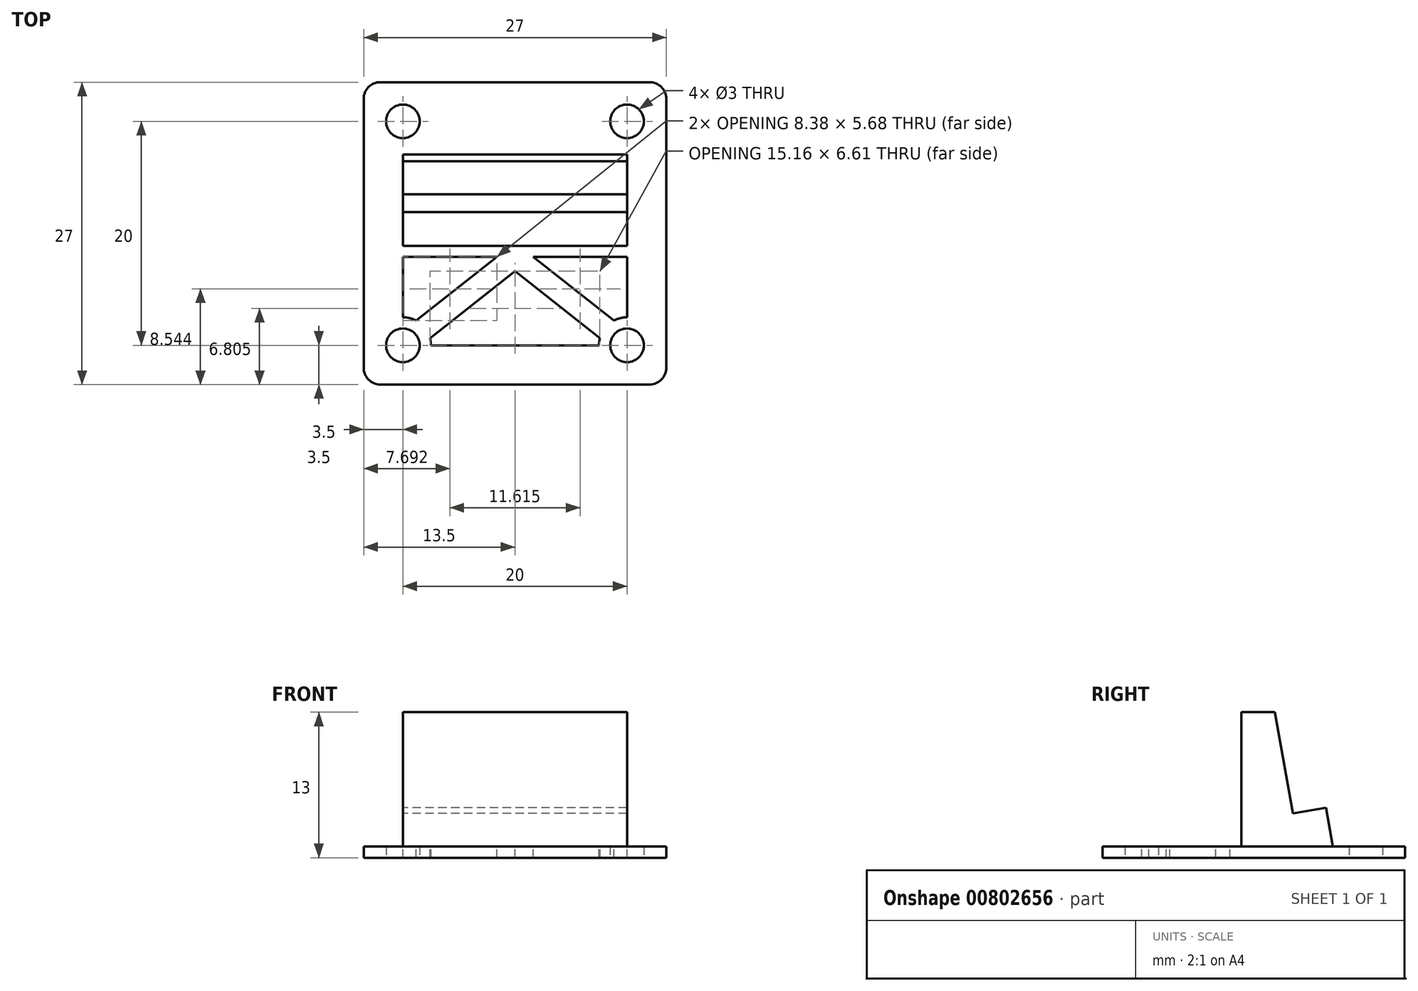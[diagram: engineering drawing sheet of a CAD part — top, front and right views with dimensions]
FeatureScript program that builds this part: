
annotation { "Feature Type Name" : "Feature", "Feature Type Description" : "" }
export const myFeature = defineFeature(function(context is Context, id is Id, definition is map)
    precondition{}
    {
        {
            var Q0;
            Q0=qCreatedBy(makeId("Top.planeOp"),FACE);
            var sketch = newSketch(context, id + "F0", { "sketchPlane" : qUnion([Q0])});
            skLineSegment(sketch, "E0.bottom", {"start": v(-12, 13.5) * mm, "end": v(12, 13.5) * mm});
            skLineSegment(sketch, "E0.top", {"start": v(-12, -13.5) * mm, "end": v(12, -13.5) * mm});
            skLineSegment(sketch, "E0.left", {"start": v(-13.5, 12) * mm, "end": v(-13.5, -12) * mm});
            skLineSegment(sketch, "E0.right", {"start": v(13.5, 12) * mm, "end": v(13.5, -12) * mm});
            skPoint(sketch, "E0.middle", {"position": v(0, 0) * mm});
            skLineSegment(sketch, "E1.bottom", {"start": v(-10, 10) * mm, "end": v(10, 10) * mm, "construction": true});
            skLineSegment(sketch, "E1.top", {"start": v(-10, -10) * mm, "end": v(10, -10) * mm, "construction": true});
            skLineSegment(sketch, "E1.left", {"start": v(-10, 10) * mm, "end": v(-10, -10) * mm, "construction": true});
            skLineSegment(sketch, "E1.right", {"start": v(10, 10) * mm, "end": v(10, -10) * mm, "construction": true});
            skPoint(sketch, "E2.visualSharp", {"position": v(-13.5, 13.5) * mm});
            skArc(sketch, "E2.filletArc", {"start": v(-12, 13.5) * mm, "mid": v(-13.06, 13.06) * mm, "end": v(-13.5, 12) * mm});
            skPoint(sketch, "E3.visualSharp", {"position": v(13.5, 13.5) * mm});
            skArc(sketch, "E3.filletArc", {"start": v(13.5, 12) * mm, "mid": v(13.06, 13.06) * mm, "end": v(12, 13.5) * mm});
            skPoint(sketch, "E4.visualSharp", {"position": v(13.5, -13.5) * mm});
            skArc(sketch, "E4.filletArc", {"start": v(12, -13.5) * mm, "mid": v(13.06, -13.06) * mm, "end": v(13.5, -12) * mm});
            skPoint(sketch, "E5.visualSharp", {"position": v(-13.5, -13.5) * mm});
            skArc(sketch, "E5.filletArc", {"start": v(-13.5, -12) * mm, "mid": v(-13.06, -13.06) * mm, "end": v(-12, -13.5) * mm});
            skSolve(sketch);
        }
        {
            var Q0;
            Q0=makeQuery(id+"F0.imprint","IMPRINT",FACE,{"disambiguationData":[TD([[makeQuery(id+"F0.imprint","IMPRINT",EDGE,{"derivedFrom":sQuery(id+"F0.wireOp",EDGE,"E0.bottom")}),-1.0]])]});
            extrude(context, id + "F1", {"entities" : qUnion([Q0]), "depth" : 1 * mm, "offsetDistance" : 25 * mm});
        }
        {
            var Q0;
            Q0=qCreatedBy(makeId("Right.planeOp"),FACE);
            var sketch = newSketch(context, id + "F2", { "sketchPlane" : qUnion([Q0])});
            skLineSegment(sketch, "E6", {"start": v(3.48, 3.95) * mm, "end": v(1.88, 13) * mm});
            skLineSegment(sketch, "E7", {"start": v(4, 1) * mm, "end": v(7.89, 1) * mm});
            skLineSegment(sketch, "E8", {"start": v(3.48, 3.95) * mm, "end": v(6.43, 4.48) * mm});
            skLineSegment(sketch, "E9", {"start": v(1.88, 13) * mm, "end": v(-1.12, 13) * mm});
            skLineSegment(sketch, "E10", {"start": v(-1.12, 13) * mm, "end": v(-1.12, 1) * mm});
            skLineSegment(sketch, "E11", {"start": v(-1.12, 1) * mm, "end": v(7.89, 1) * mm});
            skLineSegment(sketch, "E12", {"start": v(6.43, 4.48) * mm, "end": v(7.05, 1) * mm});
            skLineSegment(sketch, "E13", {"start": v(7.05, 1) * mm, "end": v(4, 1) * mm});
            skSolve(sketch);
        }
        {
            var Q0;
            Q0=makeQuery(id+"F2.imprint","IMPRINT",FACE,{"disambiguationData":[TD([[makeQuery(id+"F2.imprint","IMPRINT",EDGE,{"derivedFrom":sQuery(id+"F2.wireOp",EDGE,"E6")}),1.0]])]});
            extrude(context, id + "F3", {"entities" : qUnion([Q0]), "operationType" : NewBodyOperationType.ADD, "endBound" : BoundingType.SYMMETRIC, "depth" : 20 * mm, "offsetDistance" : 25 * mm});
        }
        {
            var Q0;
            Q0=sQuery(id+"F0.wireOp",VERTEX,"E1.top.end");
            var Q1;
            Q1=sQuery(id+"F0.wireOp",VERTEX,"E1.top.start");
            var Q2;
            Q2=sQuery(id+"F0.wireOp",VERTEX,"E1.bottom.start");
            var Q3;
            Q3=sQuery(id+"F0.wireOp",VERTEX,"E1.bottom.end");
            var Q4;
            Q4=makeQuery(id+"F1.opExtrude","SWEPT_BODY",BODY,{"disambiguationData":[OSD([sQuery(id+"F0.wireOp",EDGE,"E0.bottom"),sQuery(id+"F0.wireOp",EDGE,"E0.top"),sQuery(id+"F0.wireOp",EDGE,"E0.left"),sQuery(id+"F0.wireOp",EDGE,"E0.right"),sQuery(id+"F0.wireOp",EDGE,"E2.filletArc"),sQuery(id+"F0.wireOp",EDGE,"E3.filletArc"),sQuery(id+"F0.wireOp",EDGE,"E4.filletArc"),sQuery(id+"F0.wireOp",EDGE,"E5.filletArc")])]});
            hole(context, id + "F4", {"style" : HoleStyle.SIMPLE, "endStyle" : HoleEndStyle.BLIND, "oppositeDirection" : true, "holeDiameter" : 3 * mm, "majorDiameter" : 5 * mm, "holeDepth" : 5 * mm, "isTappedThrough" : true, "tappedDepth" : 12 * mm, "tapClearance" : 3, "locations" : qUnion([Q0, Q1, Q2, Q3]), "scope" : qUnion([Q4])});
        }
        {
            var Q0;
            Q0=makeQuery(id+"F1.opExtrude","CAP_FACE",FACE,{"disambiguationData":[OSD([sQuery(id+"F0.wireOp",EDGE,"E0.bottom"),sQuery(id+"F0.wireOp",EDGE,"E0.top"),sQuery(id+"F0.wireOp",EDGE,"E0.left"),sQuery(id+"F0.wireOp",EDGE,"E0.right"),sQuery(id+"F0.wireOp",EDGE,"E2.filletArc"),sQuery(id+"F0.wireOp",EDGE,"E3.filletArc"),sQuery(id+"F0.wireOp",EDGE,"E4.filletArc"),sQuery(id+"F0.wireOp",EDGE,"E5.filletArc")])],"isStart":false});
            var sketch = newSketch(context, id + "F5", { "sketchPlane" : qUnion([Q0])});
            skLineSegment(sketch, "E14.bottom", {"start": v(-7.5, -10) * mm, "end": v(7.5, -10) * mm});
            skLineSegment(sketch, "E14.top", {"start": v(-10, -2.12) * mm, "end": v(-1.62, -2.12) * mm});
            skLineSegment(sketch, "E14.left", {"start": v(-10, -7.5) * mm, "end": v(-10, -2.12) * mm});
            skLineSegment(sketch, "E14.right", {"start": v(10, -7.5) * mm, "end": v(10, -2.12) * mm});
            skArc(sketch, "E15", {"start": v(-7.5, -10) * mm, "mid": v(-7.52, -9.68) * mm, "end": v(-7.58, -9.37) * mm});
            skArc(sketch, "E16", {"start": v(10, -7.5) * mm, "mid": v(9.4, -7.58) * mm, "end": v(8.82, -7.8) * mm});
            skLineSegment(sketch, "E17", {"start": v(0, -2.12) * mm, "end": v(-10, -10) * mm, "construction": true});
            skLineSegment(sketch, "E18", {"start": v(0, -2.12) * mm, "end": v(10, -10) * mm, "construction": true});
            skLineSegment(sketch, "E19.0", {"start": v(-1.62, -2.12) * mm, "end": v(-8.82, -7.8) * mm});
            skLineSegment(sketch, "E20.0", {"start": v(0, -3.39) * mm, "end": v(-7.58, -9.37) * mm});
            skLineSegment(sketch, "E21.0", {"start": v(0, -3.39) * mm, "end": v(7.58, -9.37) * mm});
            skLineSegment(sketch, "E22.0", {"start": v(1.62, -2.12) * mm, "end": v(8.82, -7.8) * mm});
            skArc(sketch, "E23.trimOffspring", {"start": v(-8.82, -7.8) * mm, "mid": v(-9.4, -7.58) * mm, "end": v(-10, -7.5) * mm});
            skLineSegment(sketch, "E24.trimOffspring", {"start": v(1.62, -2.12) * mm, "end": v(10, -2.12) * mm});
            skArc(sketch, "E25.trimOffspring", {"start": v(7.58, -9.37) * mm, "mid": v(7.52, -9.68) * mm, "end": v(7.5, -10) * mm});
            skSolve(sketch);
        }
        {
            var Q0;
            Q0=makeQuery(id+"F5.imprint","IMPRINT",FACE,{"disambiguationData":[TD([[makeQuery(id+"F5.imprint","IMPRINT",EDGE,{"derivedFrom":sQuery(id+"F5.wireOp",EDGE,"E14.top")}),-1.0]])]});
            var Q1;
            Q1=makeQuery(id+"F5.imprint","IMPRINT",FACE,{"disambiguationData":[TD([[makeQuery(id+"F5.imprint","IMPRINT",EDGE,{"derivedFrom":sQuery(id+"F5.wireOp",EDGE,"E14.bottom")}),1.0]])]});
            var Q2;
            Q2=makeQuery(id+"F5.imprint","IMPRINT",FACE,{"disambiguationData":[TD([[makeQuery(id+"F5.imprint","IMPRINT",EDGE,{"derivedFrom":sQuery(id+"F5.wireOp",EDGE,"E14.right")}),1.0]])]});
            extrude(context, id + "F6", {"entities" : qUnion([Q0, Q1, Q2]), "operationType" : NewBodyOperationType.REMOVE, "oppositeDirection" : true, "depth" : 25 * mm, "offsetDistance" : 25 * mm});
        }
    });
